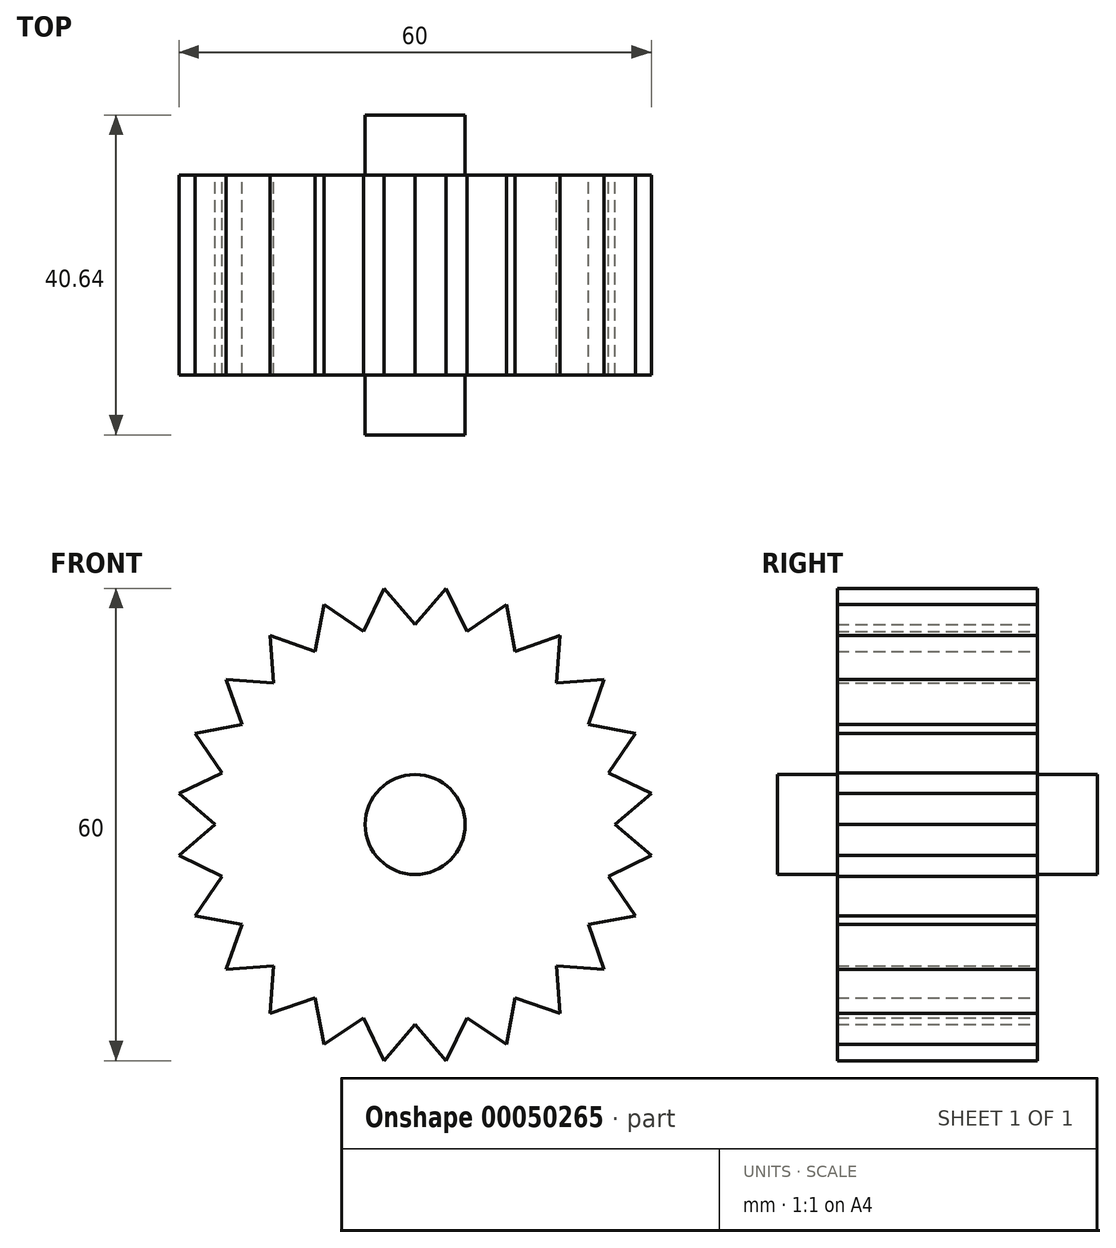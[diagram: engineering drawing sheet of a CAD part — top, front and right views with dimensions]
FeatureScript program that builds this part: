
annotation { "Feature Type Name" : "Feature", "Feature Type Description" : "" }
export const myFeature = defineFeature(function(context is Context, id is Id, definition is map)
    precondition{}
    {
        {
            var Q0;
            Q0=qCreatedBy(makeId("Front.planeOp"),FACE);
            var sketch = newSketch(context, id + "F0", { "sketchPlane" : qUnion([Q0])});
            skCircle(sketch, "E0", {"center": v(0, 0) * mm, "radius": 25.4 * mm});
            skLineSegment(sketch, "E1", {"start": v(0, 0) * mm, "end": v(25.4, 0) * mm});
            skLineSegment(sketch, "E2", {"start": v(0, 0) * mm, "end": v(0, 25.4) * mm});
            skLineSegment(sketch, "E3", {"start": v(0, 0) * mm, "end": v(-25.4, 0) * mm});
            skLineSegment(sketch, "E4", {"start": v(0, 0) * mm, "end": v(0, -25.4) * mm});
            skLineSegment(sketch, "E5", {"start": v(0, 0) * mm, "end": v(24.53, -6.57) * mm});
            skLineSegment(sketch, "E6", {"start": v(25.4, 0) * mm, "end": v(24.53, -6.57) * mm});
            skLineSegment(sketch, "E7", {"start": v(24.97, -3.29) * mm, "end": v(30, -3.95) * mm});
            skLineSegment(sketch, "E8", {"start": v(25.4, 0) * mm, "end": v(30, -3.95) * mm});
            skLineSegment(sketch, "E9", {"start": v(24.53, -6.57) * mm, "end": v(30, -3.95) * mm});
            skLineSegment(sketch, "E10", {"start": v(0, 0) * mm, "end": v(24.53, 6.57) * mm});
            skLineSegment(sketch, "E11", {"start": v(0, 0) * mm, "end": v(22, 12.7) * mm});
            skLineSegment(sketch, "E12", {"start": v(0, 0) * mm, "end": v(17.96, 17.96) * mm});
            skLineSegment(sketch, "E13", {"start": v(0, 0) * mm, "end": v(12.7, 22) * mm});
            skLineSegment(sketch, "E14", {"start": v(0, 0) * mm, "end": v(6.57, 24.53) * mm});
            skLineSegment(sketch, "E15", {"start": v(0, 0) * mm, "end": v(-6.57, -24.53) * mm});
            skLineSegment(sketch, "E16", {"start": v(0, 0) * mm, "end": v(22, -12.7) * mm});
            skLineSegment(sketch, "E17", {"start": v(0, 0) * mm, "end": v(17.96, -17.96) * mm});
            skLineSegment(sketch, "E18", {"start": v(0, 0) * mm, "end": v(12.7, -22) * mm});
            skLineSegment(sketch, "E19", {"start": v(0, 0) * mm, "end": v(6.57, -24.53) * mm});
            skLineSegment(sketch, "E20", {"start": v(0, 0) * mm, "end": v(-12.7, -22) * mm});
            skLineSegment(sketch, "E21", {"start": v(0, 0) * mm, "end": v(-17.96, -17.96) * mm});
            skLineSegment(sketch, "E22", {"start": v(0, 0) * mm, "end": v(-22, -12.7) * mm});
            skLineSegment(sketch, "E23", {"start": v(0, 0) * mm, "end": v(-24.53, -6.57) * mm});
            skLineSegment(sketch, "E24", {"start": v(0, 0) * mm, "end": v(-24.53, 6.57) * mm});
            skLineSegment(sketch, "E25", {"start": v(0, 0) * mm, "end": v(-22, 12.7) * mm});
            skLineSegment(sketch, "E26", {"start": v(0, 0) * mm, "end": v(-17.96, 17.96) * mm});
            skLineSegment(sketch, "E27", {"start": v(0, 0) * mm, "end": v(-12.7, 22) * mm});
            skLineSegment(sketch, "E28", {"start": v(0, 0) * mm, "end": v(-6.57, 24.53) * mm});
            skLineSegment(sketch, "E29", {"start": v(25.4, 0) * mm, "end": v(24.53, 6.57) * mm});
            skLineSegment(sketch, "E30", {"start": v(22, 12.7) * mm, "end": v(17.96, 17.96) * mm});
            skLineSegment(sketch, "E31", {"start": v(12.7, 22) * mm, "end": v(6.57, 24.53) * mm});
            skLineSegment(sketch, "E32", {"start": v(0, 25.4) * mm, "end": v(-6.57, 24.53) * mm});
            skLineSegment(sketch, "E33", {"start": v(-12.7, 22) * mm, "end": v(-17.96, 17.96) * mm});
            skLineSegment(sketch, "E34", {"start": v(-22, 12.7) * mm, "end": v(-24.53, 6.57) * mm});
            skLineSegment(sketch, "E35", {"start": v(-25.4, 0) * mm, "end": v(-24.53, -6.57) * mm});
            skLineSegment(sketch, "E36", {"start": v(-22, -12.7) * mm, "end": v(-17.96, -17.96) * mm});
            skLineSegment(sketch, "E37", {"start": v(-12.7, -22) * mm, "end": v(-6.57, -24.53) * mm});
            skLineSegment(sketch, "E38", {"start": v(0, -25.4) * mm, "end": v(6.57, -24.53) * mm});
            skLineSegment(sketch, "E39", {"start": v(12.7, -22) * mm, "end": v(17.96, -17.96) * mm});
            skLineSegment(sketch, "E40", {"start": v(22, -12.7) * mm, "end": v(24.53, -6.57) * mm});
            skLineSegment(sketch, "E41", {"start": v(24.53, 6.57) * mm, "end": v(22, 12.7) * mm});
            skLineSegment(sketch, "E42", {"start": v(17.96, 17.96) * mm, "end": v(12.7, 22) * mm});
            skLineSegment(sketch, "E43", {"start": v(6.57, 24.53) * mm, "end": v(0, 25.4) * mm});
            skLineSegment(sketch, "E44", {"start": v(-6.57, 24.53) * mm, "end": v(-12.7, 22) * mm});
            skLineSegment(sketch, "E45", {"start": v(-17.96, 17.96) * mm, "end": v(-22, 12.7) * mm});
            skLineSegment(sketch, "E46", {"start": v(-24.53, 6.57) * mm, "end": v(-25.4, 0) * mm});
            skLineSegment(sketch, "E47", {"start": v(-24.53, -6.57) * mm, "end": v(-22, -12.7) * mm});
            skLineSegment(sketch, "E48", {"start": v(-17.96, -17.96) * mm, "end": v(-12.7, -22) * mm});
            skLineSegment(sketch, "E49", {"start": v(-6.57, -24.53) * mm, "end": v(0, -25.4) * mm});
            skLineSegment(sketch, "E50", {"start": v(6.57, -24.53) * mm, "end": v(12.7, -22) * mm});
            skLineSegment(sketch, "E51", {"start": v(17.96, -17.96) * mm, "end": v(22, -12.7) * mm});
            skLineSegment(sketch, "E52", {"start": v(24.97, 3.29) * mm, "end": v(30, 3.95) * mm});
            skLineSegment(sketch, "E53", {"start": v(30, 3.95) * mm, "end": v(24.53, 6.57) * mm});
            skLineSegment(sketch, "E54", {"start": v(30, 3.95) * mm, "end": v(25.4, 0) * mm});
            skPoint(sketch, "E55.startSnap0", {"position": v(23.27, 9.64) * mm});
            skLineSegment(sketch, "E56", {"start": v(23.27, 9.64) * mm, "end": v(27.96, 11.58) * mm});
            skLineSegment(sketch, "E57", {"start": v(27.96, 11.58) * mm, "end": v(22, 12.7) * mm});
            skLineSegment(sketch, "E58", {"start": v(24.53, 6.57) * mm, "end": v(27.96, 11.58) * mm});
            skLineSegment(sketch, "E59", {"start": v(19.98, 15.33) * mm, "end": v(24, 18.42) * mm});
            skLineSegment(sketch, "E60", {"start": v(24, 18.42) * mm, "end": v(22, 12.7) * mm});
            skLineSegment(sketch, "E61", {"start": v(24, 18.42) * mm, "end": v(17.96, 17.96) * mm});
            skLineSegment(sketch, "E62", {"start": v(15.33, 19.98) * mm, "end": v(18.42, 24) * mm});
            skLineSegment(sketch, "E63", {"start": v(18.42, 24) * mm, "end": v(17.96, 17.96) * mm});
            skLineSegment(sketch, "E64", {"start": v(18.42, 24) * mm, "end": v(12.7, 22) * mm});
            skLineSegment(sketch, "E65", {"start": v(9.64, 23.27) * mm, "end": v(11.58, 27.96) * mm});
            skLineSegment(sketch, "E66", {"start": v(11.58, 27.96) * mm, "end": v(12.7, 22) * mm});
            skLineSegment(sketch, "E67", {"start": v(11.58, 27.96) * mm, "end": v(6.57, 24.53) * mm});
            skLineSegment(sketch, "E68", {"start": v(3.29, 24.97) * mm, "end": v(3.95, 30) * mm});
            skLineSegment(sketch, "E69", {"start": v(3.95, 30) * mm, "end": v(6.57, 24.53) * mm});
            skLineSegment(sketch, "E70", {"start": v(3.95, 30) * mm, "end": v(0, 25.4) * mm});
            skLineSegment(sketch, "E71", {"start": v(-3.29, 24.97) * mm, "end": v(-3.95, 30) * mm});
            skLineSegment(sketch, "E72", {"start": v(-3.95, 30) * mm, "end": v(0, 25.4) * mm});
            skLineSegment(sketch, "E73", {"start": v(-3.95, 30) * mm, "end": v(-6.57, 24.53) * mm});
            skLineSegment(sketch, "E74", {"start": v(-9.64, 23.27) * mm, "end": v(-11.58, 27.96) * mm});
            skLineSegment(sketch, "E75", {"start": v(-11.58, 27.96) * mm, "end": v(-6.57, 24.53) * mm});
            skLineSegment(sketch, "E76", {"start": v(-11.58, 27.96) * mm, "end": v(-12.7, 22) * mm});
            skLineSegment(sketch, "E77", {"start": v(-15.33, 19.98) * mm, "end": v(-18.42, 24) * mm});
            skLineSegment(sketch, "E78", {"start": v(-18.42, 24) * mm, "end": v(-17.96, 17.96) * mm});
            skLineSegment(sketch, "E79", {"start": v(-12.7, 22) * mm, "end": v(-18.42, 24) * mm});
            skLineSegment(sketch, "E80", {"start": v(-19.98, 15.33) * mm, "end": v(-24, 18.42) * mm});
            skLineSegment(sketch, "E81", {"start": v(-24, 18.42) * mm, "end": v(-22, 12.7) * mm});
            skLineSegment(sketch, "E82", {"start": v(-17.96, 17.96) * mm, "end": v(-24, 18.42) * mm});
            skLineSegment(sketch, "E83", {"start": v(-23.27, 9.64) * mm, "end": v(-27.96, 11.58) * mm});
            skLineSegment(sketch, "E84", {"start": v(-27.96, 11.58) * mm, "end": v(-22, 12.7) * mm});
            skLineSegment(sketch, "E85", {"start": v(-27.96, 11.58) * mm, "end": v(-24.53, 6.57) * mm});
            skLineSegment(sketch, "E86", {"start": v(-24.97, 3.29) * mm, "end": v(-30, 3.95) * mm});
            skLineSegment(sketch, "E87", {"start": v(-30, 3.95) * mm, "end": v(-25.4, 0) * mm});
            skLineSegment(sketch, "E88", {"start": v(-30, 3.95) * mm, "end": v(-24.53, 6.57) * mm});
            skLineSegment(sketch, "E89", {"start": v(-24.97, -3.29) * mm, "end": v(-30, -3.95) * mm});
            skLineSegment(sketch, "E90", {"start": v(-30, -3.95) * mm, "end": v(-24.53, -6.57) * mm});
            skLineSegment(sketch, "E91", {"start": v(-30, -3.95) * mm, "end": v(-25.4, 0) * mm});
            skLineSegment(sketch, "E92", {"start": v(-23.27, -9.64) * mm, "end": v(-27.96, -11.58) * mm});
            skLineSegment(sketch, "E93", {"start": v(-27.96, -11.58) * mm, "end": v(-24.53, -6.57) * mm});
            skLineSegment(sketch, "E94", {"start": v(-22, -12.7) * mm, "end": v(-27.96, -11.58) * mm});
            skLineSegment(sketch, "E95", {"start": v(-19.98, -15.33) * mm, "end": v(-24, -18.42) * mm});
            skLineSegment(sketch, "E96", {"start": v(-24, -18.42) * mm, "end": v(-22, -12.7) * mm});
            skLineSegment(sketch, "E97", {"start": v(-17.96, -17.96) * mm, "end": v(-24, -18.42) * mm});
            skLineSegment(sketch, "E98", {"start": v(-15.33, -19.98) * mm, "end": v(-18.42, -24) * mm});
            skLineSegment(sketch, "E99", {"start": v(-18.42, -24) * mm, "end": v(-17.96, -17.96) * mm});
            skLineSegment(sketch, "E100", {"start": v(-12.7, -22) * mm, "end": v(-18.42, -24) * mm});
            skLineSegment(sketch, "E101", {"start": v(-9.64, -23.27) * mm, "end": v(-11.58, -27.96) * mm});
            skLineSegment(sketch, "E102", {"start": v(-11.58, -27.96) * mm, "end": v(-12.7, -22) * mm});
            skLineSegment(sketch, "E103", {"start": v(-6.57, -24.53) * mm, "end": v(-11.58, -27.96) * mm});
            skLineSegment(sketch, "E104", {"start": v(-3.29, -24.97) * mm, "end": v(-3.95, -30) * mm});
            skLineSegment(sketch, "E105", {"start": v(-3.95, -30) * mm, "end": v(-6.57, -24.53) * mm});
            skLineSegment(sketch, "E106", {"start": v(0, -25.4) * mm, "end": v(-3.95, -30) * mm});
            skLineSegment(sketch, "E107", {"start": v(3.29, -24.97) * mm, "end": v(3.95, -30) * mm});
            skLineSegment(sketch, "E108", {"start": v(3.95, -30) * mm, "end": v(0, -25.4) * mm});
            skLineSegment(sketch, "E109", {"start": v(6.57, -24.53) * mm, "end": v(3.95, -30) * mm});
            skLineSegment(sketch, "E110", {"start": v(9.64, -23.27) * mm, "end": v(11.58, -27.96) * mm});
            skLineSegment(sketch, "E111", {"start": v(12.7, -22) * mm, "end": v(11.58, -27.96) * mm});
            skLineSegment(sketch, "E112", {"start": v(11.58, -27.96) * mm, "end": v(6.57, -24.53) * mm});
            skLineSegment(sketch, "E113", {"start": v(15.33, -19.98) * mm, "end": v(18.42, -24) * mm});
            skLineSegment(sketch, "E114", {"start": v(18.42, -24) * mm, "end": v(12.7, -22) * mm});
            skLineSegment(sketch, "E115", {"start": v(17.96, -17.96) * mm, "end": v(18.42, -24) * mm});
            skLineSegment(sketch, "E116", {"start": v(19.98, -15.33) * mm, "end": v(24, -18.42) * mm});
            skLineSegment(sketch, "E117", {"start": v(24, -18.42) * mm, "end": v(17.96, -17.96) * mm});
            skLineSegment(sketch, "E118", {"start": v(22, -12.7) * mm, "end": v(24, -18.42) * mm});
            skLineSegment(sketch, "E119", {"start": v(23.27, -9.64) * mm, "end": v(27.96, -11.58) * mm});
            skLineSegment(sketch, "E120", {"start": v(27.96, -11.58) * mm, "end": v(22, -12.7) * mm});
            skLineSegment(sketch, "E121", {"start": v(24.53, -6.57) * mm, "end": v(27.96, -11.58) * mm});
            skSolve(sketch);
        }
        {
            var Q0;
            Q0=qSketchRegion(id+"F0",true);
            extrude(context, id + "F1", {"entities" : qUnion([Q0]), "depth" : 25.4 * mm});
        }
        {
            var Q0;
            Q0=makeQuery(id+"F1.opExtrude","CAP_FACE",FACE,{"disambiguationData":[OSD([sQuery(id+"F0.wireOp",EDGE,"E8"),sQuery(id+"F0.wireOp",EDGE,"E9"),sQuery(id+"F0.wireOp",EDGE,"E53"),sQuery(id+"F0.wireOp",EDGE,"E54"),sQuery(id+"F0.wireOp",EDGE,"E57"),sQuery(id+"F0.wireOp",EDGE,"E58"),sQuery(id+"F0.wireOp",EDGE,"E60"),sQuery(id+"F0.wireOp",EDGE,"E61"),sQuery(id+"F0.wireOp",EDGE,"E63"),sQuery(id+"F0.wireOp",EDGE,"E64"),sQuery(id+"F0.wireOp",EDGE,"E66"),sQuery(id+"F0.wireOp",EDGE,"E67"),sQuery(id+"F0.wireOp",EDGE,"E69"),sQuery(id+"F0.wireOp",EDGE,"E70"),sQuery(id+"F0.wireOp",EDGE,"E72"),sQuery(id+"F0.wireOp",EDGE,"E73"),sQuery(id+"F0.wireOp",EDGE,"E75"),sQuery(id+"F0.wireOp",EDGE,"E76"),sQuery(id+"F0.wireOp",EDGE,"E78"),sQuery(id+"F0.wireOp",EDGE,"E79"),sQuery(id+"F0.wireOp",EDGE,"E81"),sQuery(id+"F0.wireOp",EDGE,"E82"),sQuery(id+"F0.wireOp",EDGE,"E84"),sQuery(id+"F0.wireOp",EDGE,"E85"),sQuery(id+"F0.wireOp",EDGE,"E87"),sQuery(id+"F0.wireOp",EDGE,"E88"),sQuery(id+"F0.wireOp",EDGE,"E90"),sQuery(id+"F0.wireOp",EDGE,"E91"),sQuery(id+"F0.wireOp",EDGE,"E93"),sQuery(id+"F0.wireOp",EDGE,"E94"),sQuery(id+"F0.wireOp",EDGE,"E96"),sQuery(id+"F0.wireOp",EDGE,"E97"),sQuery(id+"F0.wireOp",EDGE,"E99"),sQuery(id+"F0.wireOp",EDGE,"E100"),sQuery(id+"F0.wireOp",EDGE,"E102"),sQuery(id+"F0.wireOp",EDGE,"E103"),sQuery(id+"F0.wireOp",EDGE,"E105"),sQuery(id+"F0.wireOp",EDGE,"E106"),sQuery(id+"F0.wireOp",EDGE,"E108"),sQuery(id+"F0.wireOp",EDGE,"E109"),sQuery(id+"F0.wireOp",EDGE,"E111"),sQuery(id+"F0.wireOp",EDGE,"E112"),sQuery(id+"F0.wireOp",EDGE,"E114"),sQuery(id+"F0.wireOp",EDGE,"E115"),sQuery(id+"F0.wireOp",EDGE,"E117"),sQuery(id+"F0.wireOp",EDGE,"E118"),sQuery(id+"F0.wireOp",EDGE,"E120"),sQuery(id+"F0.wireOp",EDGE,"E121")])],"isStart":false});
            var sketch = newSketch(context, id + "F2", { "sketchPlane" : qUnion([Q0])});
            skCircle(sketch, "E122", {"center": v(0, 0) * mm, "radius": 6.35 * mm});
            skSolve(sketch);
        }
        {
            var Q0;
            Q0=makeQuery(id+"F2.imprint","IMPRINT",FACE,{"disambiguationData":[TD([[makeQuery(id+"F2.imprint","IMPRINT",EDGE,{"derivedFrom":sQuery(id+"F2.wireOp",EDGE,"E122")}),1.0]])]});
            extrude(context, id + "F3", {"entities" : qUnion([Q0]), "operationType" : NewBodyOperationType.ADD, "depth" : 7.62 * mm});
        }
        {
            var Q0;
            Q0=makeQuery(id+"F1.opExtrude","CAP_FACE",FACE,{"disambiguationData":[OSD([sQuery(id+"F0.wireOp",EDGE,"E8"),sQuery(id+"F0.wireOp",EDGE,"E9"),sQuery(id+"F0.wireOp",EDGE,"E53"),sQuery(id+"F0.wireOp",EDGE,"E54"),sQuery(id+"F0.wireOp",EDGE,"E57"),sQuery(id+"F0.wireOp",EDGE,"E58"),sQuery(id+"F0.wireOp",EDGE,"E60"),sQuery(id+"F0.wireOp",EDGE,"E61"),sQuery(id+"F0.wireOp",EDGE,"E63"),sQuery(id+"F0.wireOp",EDGE,"E64"),sQuery(id+"F0.wireOp",EDGE,"E66"),sQuery(id+"F0.wireOp",EDGE,"E67"),sQuery(id+"F0.wireOp",EDGE,"E69"),sQuery(id+"F0.wireOp",EDGE,"E70"),sQuery(id+"F0.wireOp",EDGE,"E72"),sQuery(id+"F0.wireOp",EDGE,"E73"),sQuery(id+"F0.wireOp",EDGE,"E75"),sQuery(id+"F0.wireOp",EDGE,"E76"),sQuery(id+"F0.wireOp",EDGE,"E78"),sQuery(id+"F0.wireOp",EDGE,"E79"),sQuery(id+"F0.wireOp",EDGE,"E81"),sQuery(id+"F0.wireOp",EDGE,"E82"),sQuery(id+"F0.wireOp",EDGE,"E84"),sQuery(id+"F0.wireOp",EDGE,"E85"),sQuery(id+"F0.wireOp",EDGE,"E87"),sQuery(id+"F0.wireOp",EDGE,"E88"),sQuery(id+"F0.wireOp",EDGE,"E90"),sQuery(id+"F0.wireOp",EDGE,"E91"),sQuery(id+"F0.wireOp",EDGE,"E93"),sQuery(id+"F0.wireOp",EDGE,"E94"),sQuery(id+"F0.wireOp",EDGE,"E96"),sQuery(id+"F0.wireOp",EDGE,"E97"),sQuery(id+"F0.wireOp",EDGE,"E99"),sQuery(id+"F0.wireOp",EDGE,"E100"),sQuery(id+"F0.wireOp",EDGE,"E102"),sQuery(id+"F0.wireOp",EDGE,"E103"),sQuery(id+"F0.wireOp",EDGE,"E105"),sQuery(id+"F0.wireOp",EDGE,"E106"),sQuery(id+"F0.wireOp",EDGE,"E108"),sQuery(id+"F0.wireOp",EDGE,"E109"),sQuery(id+"F0.wireOp",EDGE,"E111"),sQuery(id+"F0.wireOp",EDGE,"E112"),sQuery(id+"F0.wireOp",EDGE,"E114"),sQuery(id+"F0.wireOp",EDGE,"E115"),sQuery(id+"F0.wireOp",EDGE,"E117"),sQuery(id+"F0.wireOp",EDGE,"E118"),sQuery(id+"F0.wireOp",EDGE,"E120"),sQuery(id+"F0.wireOp",EDGE,"E121")])],"isStart":true});
            var sketch = newSketch(context, id + "F4", { "sketchPlane" : qUnion([Q0])});
            skCircle(sketch, "E123", {"center": v(0, 0) * mm, "radius": 6.35 * mm});
            skSolve(sketch);
        }
        {
            var Q0;
            Q0 = qSketchRegion(id + "F4", true);
            extrude(context, id + "F5", {"entities" : qUnion([Q0]), "operationType" : NewBodyOperationType.ADD, "depth" : 7.62 * mm});
        }
    });
